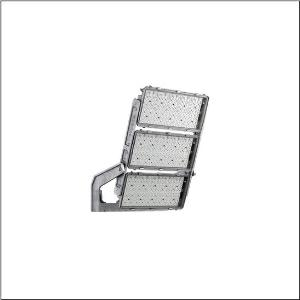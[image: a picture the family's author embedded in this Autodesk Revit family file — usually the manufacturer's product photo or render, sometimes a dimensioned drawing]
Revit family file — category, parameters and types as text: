
# Revit family: floodlight_fl_11_maxi_pro_remote___pl64_5xa779425v01aa_e912
name_source: partatom
category: Lighting Fixtures
units: mm (PartAtom-declared; Revit-internal decimal feet)

## family parameters
Cut with Voids When Loaded = No
Host = Face
Light Source = No
Part Type = Normal
Room Calculation Point = No
Round Connector Dimension = Use Diameter
Shared = No

## types (1)
- --- (1 x LED, 206660 lm, 1539.3 W, 3000K)
    Apparent Load = 1539 VA
    CIE Flux Codes = 28 79 98 100 100
    Color Rendering = 70
    Color Temperature = 3000K
    Default Elevation = 1800 mm
    Description = Floodlight FL 11  maxi  pro Remote floodlight; light control with lens of PMMA; cover panel of toughened safety glass, transparent; light distribution: PL64, asymmetric direct distribution, LEDcolour temperature: 3000K, rated luminous flux: 206.660lm, colour rendering: CRI > 70, light colour: 730; luminous efficacy: 134lm/W; brightness control: DALI 2 (1 DALI address); with terminal, 8-pole, max. 2.5mm², mains connection: 220..240V/380..400V AC, 50/60Hz, surge voltage resistance: line to ground: 10kV, ECG replaceable separately, no afterglow with DALI off / DMX off command, LED unit replaceable without ESD environment, dustproof LED module, dimming range 10..100%; 1539W floodlight with 2x LED unit of diecast aluminium, coated grey; length: 713mm / width: 651mm / height: 338mm; mounting bracket, of diecast aluminium, uncoated, natural, equipment: Power, protection rating (complete): IP66; insulation class (complete): insulation class I (protective earthing); certification: CE, ENEC, VDE; ball protection: ball impact resistance with accessories, impact resistance: IK07; only for outdoor installations, rated ambient temperature 10°C, permissible operating ambient temperature: -40..+30°C, permissible storage temperature: -40..+85°C; packaging unit: 1 piece

Light Distribution: PL64
    Height = 320 mm
    Lamp = 1 x LED
    Lamp Light Flux = 206660 lm
    Lamp Power = 1539.3 W
    Lamp count = 1
    Length = 1002 mm
    Luminous efficacy = 134 lm/W
    Manufacturer = Siteco
    ModVariant = No
    Model = 5XA779425V01AA
    Mounting Place = Ceiling
    Mounting Type = Surface mounted
    Number of Poles = 1
    OnlyDefault = Yes
    Power Factor = 1
    Product Name = Floodlight FL 11 maxi pro Remote | PL64
    Product group = floodlight | ceiling mounted
    ProductGroupID = 303
    Protection Class = Protection class I
    Protection Degree = IP 66
    RLX_Detail_Level = 1
    RLX_Emergency_Light_Flux = 0 lm
    RLX_Emergency_Type = 0
    RLX_Emergency_Type_DB = No
    RlxData = <blob elided: 52601 chars, md5=6962fcba>
    Socket = socket
    Standby Power = 0 W
    System Light Flux = 206660 lm
    System Power = 1539 W
    Type Comments = factory setting: luminous flux: 100 % | dim-lin: 254 | 1080 mA
    Type Image = l_1006784.jpg
    URL = http://relux.com
    VarID = @adj_051227
    Voltage = 0 V
    Weight = 0.00 kg
    Width = 655 mm

## geometry (parser evidence)
native form markers: Blend x4, Sweep x15
no freeform markers — native parametric forms only
